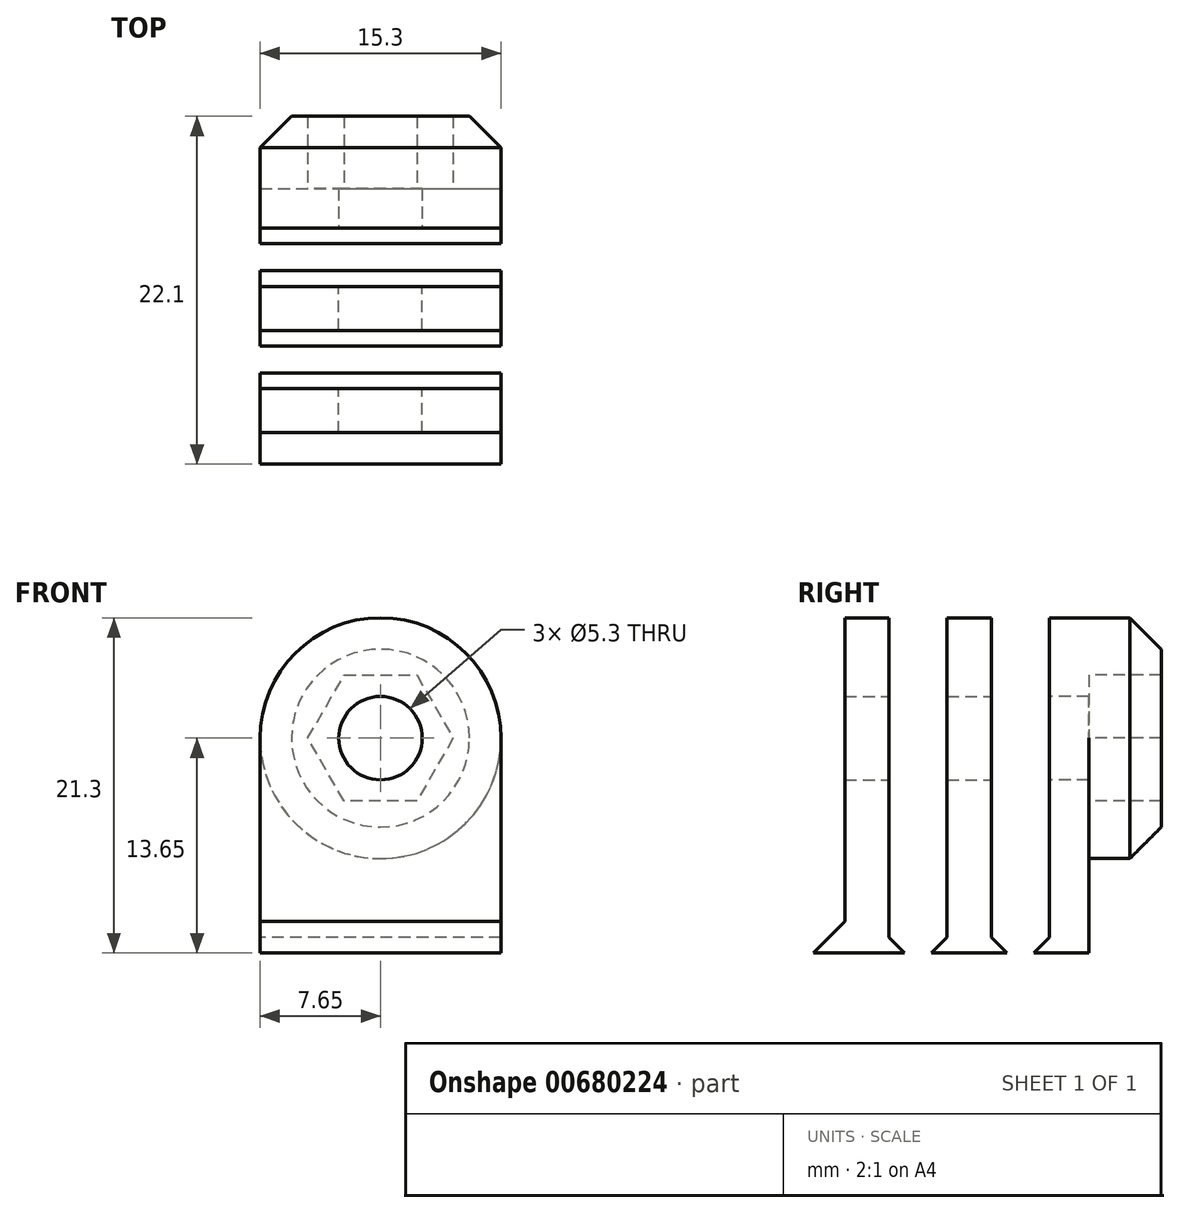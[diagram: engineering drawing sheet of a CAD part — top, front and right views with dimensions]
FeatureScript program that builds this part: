
annotation { "Feature Type Name" : "Feature", "Feature Type Description" : "" }
export const myFeature = defineFeature(function(context is Context, id is Id, definition is map)
    precondition{}
    {
        {
            var Q0;
            Q0=qCreatedBy(makeId("Front.planeOp"),FACE);
            var sketch = newSketch(context, id + "F0", { "sketchPlane" : qUnion([Q0])});
            skCircle(sketch, "E0", {"center": v(0, 0) * mm, "radius": 2.65 * mm});
            skCircle(sketch, "E1", {"center": v(0, 0) * mm, "radius": 7.65 * mm});
            skCircle(sketch, "E2.cCircle", {"center": v(0, 0) * mm, "radius": 4 * mm, "construction": true});
            skLineSegment(sketch, "E2.0", {"start": v(4.62, 0) * mm, "end": v(2.3, -4) * mm});
            skLineSegment(sketch, "E2.1", {"start": v(2.3, -4) * mm, "end": v(-2.3, -4) * mm});
            skLineSegment(sketch, "E2.2", {"start": v(-2.3, -4) * mm, "end": v(-4.62, 0) * mm});
            skLineSegment(sketch, "E2.3", {"start": v(-4.62, 0) * mm, "end": v(-2.3, 4) * mm});
            skLineSegment(sketch, "E2.4", {"start": v(-2.3, 4) * mm, "end": v(2.3, 4) * mm});
            skLineSegment(sketch, "E2.5", {"start": v(2.3, 4) * mm, "end": v(4.62, 0) * mm});
            skPoint(sketch, "E2.0.midPoint", {"position": v(3.46, -2) * mm});
            skLineSegment(sketch, "E3.top", {"start": v(-7.65, -13.65) * mm, "end": v(7.65, -13.65) * mm});
            skPoint(sketch, "E4.start.orphan", {"position": v(-7.65, 0) * mm});
            skPoint(sketch, "E5.start.orphan", {"position": v(7.65, 0) * mm});
            skLineSegment(sketch, "E6", {"start": v(-7.65, 0) * mm, "end": v(-7.65, -13.65) * mm});
            skLineSegment(sketch, "E7", {"start": v(7.65, -13.65) * mm, "end": v(7.65, 0) * mm});
            skSolve(sketch);
        }
        {
            var Q0;
            {var subQ0=sQuery(id+"F0.wireOp",EDGE,"E4");Q0=makeQuery(id+"F0.imprint","IMPRINT",FACE,{"disambiguationData":[TD([[makeQuery(id+"F0.imprint","IMPRINT",EDGE,{"derivedFrom":subQ0}),1.0]])]});}
            var Q1;
            Q1=makeQuery(id+"F0.imprint","IMPRINT",FACE,{"disambiguationData":[TD([[makeQuery(id+"F0.imprint","IMPRINT",EDGE,{"derivedFrom":sQuery(id+"F0.wireOp",EDGE,"E2.0")}),1.0]])]});
            var Q2;
            Q2=makeQuery(id+"F0.imprint","IMPRINT",FACE,{"disambiguationData":[TD([[makeQuery(id+"F0.imprint","IMPRINT",EDGE,{"derivedFrom":sQuery(id+"F0.wireOp",EDGE,"E0")}),-1.0]])]});
            var Q3;
            Q3=makeQuery(id+"F0.imprint","IMPRINT",FACE,{"disambiguationData":[TD([[makeQuery(id+"F0.imprint","IMPRINT",EDGE,{"derivedFrom":sQuery(id+"F0.wireOp",EDGE,"E3.top")}),1.0]])]});
            extrude(context, id + "F1", {"entities" : qUnion([Q0, Q1, Q2, Q3]), "endBound" : BoundingType.SYMMETRIC, "depth" : 2.8 * mm, "offsetDistance" : 25 * mm});
        }
        {
            var Q0;
            {var subQ0=sQuery(id+"F0.wireOp",EDGE,"E4");Q0=makeQuery(id+"F0.imprint","IMPRINT",FACE,{"disambiguationData":[TD([[makeQuery(id+"F0.imprint","IMPRINT",EDGE,{"derivedFrom":subQ0}),1.0]])]});}
            var Q1;
            Q1=makeQuery(id+"F0.imprint","IMPRINT",FACE,{"disambiguationData":[TD([[makeQuery(id+"F0.imprint","IMPRINT",EDGE,{"derivedFrom":sQuery(id+"F0.wireOp",EDGE,"E2.0")}),1.0]])]});
            var Q2;
            Q2=makeQuery(id+"F0.imprint","IMPRINT",FACE,{"disambiguationData":[TD([[makeQuery(id+"F0.imprint","IMPRINT",EDGE,{"derivedFrom":sQuery(id+"F0.wireOp",EDGE,"E0")}),-1.0]])]});
            var Q3;
            Q3=makeQuery(id+"F0.imprint","IMPRINT",FACE,{"disambiguationData":[TD([[makeQuery(id+"F0.imprint","IMPRINT",EDGE,{"derivedFrom":sQuery(id+"F0.wireOp",EDGE,"E3.top")}),1.0]])]});
            extrude(context, id + "F2", {"entities" : qUnion([Q0, Q1, Q2, Q3]), "depth" : 7.9 * mm, "hasSecondDirection" : true, "secondDirectionOppositeDirection" : false, "secondDirectionDepth" : 5.1 * mm, "offsetDistance" : 25 * mm});
        }
        {
            var Q0;
            Q0=makeQuery(id+"F0.imprint","IMPRINT",FACE,{"disambiguationData":[TD([[makeQuery(id+"F0.imprint","IMPRINT",EDGE,{"derivedFrom":sQuery(id+"F0.wireOp",EDGE,"E2.0")}),1.0]])]});
            var Q1;
            {var subQ0=sQuery(id+"F0.wireOp",EDGE,"E4");Q1=makeQuery(id+"F0.imprint","IMPRINT",FACE,{"disambiguationData":[TD([[makeQuery(id+"F0.imprint","IMPRINT",EDGE,{"derivedFrom":subQ0}),1.0]])]});}
            var Q2;
            Q2=makeQuery(id+"F0.imprint","IMPRINT",FACE,{"disambiguationData":[TD([[makeQuery(id+"F0.imprint","IMPRINT",EDGE,{"derivedFrom":sQuery(id+"F0.wireOp",EDGE,"E0")}),-1.0]])]});
            var Q3;
            Q3=makeQuery(id+"F0.imprint","IMPRINT",FACE,{"disambiguationData":[TD([[makeQuery(id+"F0.imprint","IMPRINT",EDGE,{"derivedFrom":sQuery(id+"F0.wireOp",EDGE,"E3.top")}),1.0]])]});
            extrude(context, id + "F3", {"entities" : qUnion([Q0, Q1, Q2, Q3]), "oppositeDirection" : true, "depth" : 7.6 * mm, "hasSecondDirection" : true, "secondDirectionOppositeDirection" : true, "secondDirectionDepth" : 5.1 * mm, "offsetDistance" : 25 * mm});
        }
        {
            var Q0;
            Q0=makeQuery(id+"F0.imprint","IMPRINT",FACE,{"disambiguationData":[TD([[makeQuery(id+"F0.imprint","IMPRINT",EDGE,{"derivedFrom":sQuery(id+"F0.wireOp",EDGE,"E2.0")}),1.0]])]});
            extrude(context, id + "F4", {"entities" : qUnion([Q0]), "operationType" : NewBodyOperationType.ADD, "oppositeDirection" : true, "depth" : 12.2 * mm, "hasSecondDirection" : true, "secondDirectionOppositeDirection" : true, "secondDirectionDepth" : 7.5 * mm});
        }
        {
            var Q0;
            Q0=makeQuery(id+"F4.opExtrude","CAP_EDGE",EDGE,{"disambiguationData":[OSD([sQuery(id+"F0.wireOp",EDGE,"E1")])],"isStart":false});
            chamfer(context, id + "F5", {"entities" : qUnion([Q0]), "width" : 2 * mm, "tangentPropagation" : true});
        }
        {
            var Q0;
            Q0=makeQuery(id+"F3.opExtrude","SWEPT_FACE",FACE,{"disambiguationData":[OSD([sQuery(id+"F0.wireOp",EDGE,"E6")])]});
            var sketch = newSketch(context, id + "F6", { "sketchPlane" : qUnion([Q0])});
            skLineSegment(sketch, "E8", {"start": v(-7.6, -13.65) * mm, "end": v(-9.6, -13.65) * mm});
            skLineSegment(sketch, "E9", {"start": v(-9.6, -13.65) * mm, "end": v(-7.6, -13.65) * mm});
            skLineSegment(sketch, "E10", {"start": v(-9.6, -13.65) * mm, "end": v(-7.6, -11.65) * mm});
            skLineSegment(sketch, "E11", {"start": v(-7.6, -11.65) * mm, "end": v(-7.6, -13.65) * mm});
            skSolve(sketch);
        }
        {
            var Q0;
            Q0=makeQuery(id+"F2.opExtrude","SWEPT_FACE",FACE,{"disambiguationData":[OSD([sQuery(id+"F0.wireOp",EDGE,"E6")])]});
            var sketch = newSketch(context, id + "F7", { "sketchPlane" : qUnion([Q0])});
            skLineSegment(sketch, "E12", {"start": v(7.9, -13.65) * mm, "end": v(9.9, -13.65) * mm});
            skLineSegment(sketch, "E13", {"start": v(9.9, -13.65) * mm, "end": v(7.9, -11.65) * mm});
            skLineSegment(sketch, "E14", {"start": v(7.9, -11.65) * mm, "end": v(7.9, -13.65) * mm});
            skSolve(sketch);
        }
        {
            var Q0;
            Q0=makeQuery(id+"F10.boolean.opBoolean","MERGE",FACE,{"derivedFrom":[makeQuery(id+"F3.opExtrude","SWEPT_FACE",FACE,{"disambiguationData":[OSD([sQuery(id+"F0.wireOp",EDGE,"E6")])]}),makeQuery(id+"F10.opExtrude","CAP_FACE",FACE,{"disambiguationData":[OSD([sQuery(id+"F6.wireOp",EDGE,"E9"),sQuery(id+"F6.wireOp",EDGE,"E10"),sQuery(id+"F6.wireOp",EDGE,"E11")])],"isStart":true})]});
            var sketch = newSketch(context, id + "F8", { "sketchPlane" : qUnion([Q0])});
            skLineSegment(sketch, "E15", {"start": v(-5.1, -13.65) * mm, "end": v(-4.1, -13.65) * mm});
            skLineSegment(sketch, "E16", {"start": v(-4.1, -13.65) * mm, "end": v(-5.1, -12.65) * mm});
            skLineSegment(sketch, "E17", {"start": v(-5.1, -12.65) * mm, "end": v(-5.1, -13.65) * mm});
            skSolve(sketch);
        }
        {
            var Q0;
            Q0=makeQuery(id+"F1.opExtrude","SWEPT_FACE",FACE,{"disambiguationData":[OSD([sQuery(id+"F0.wireOp",EDGE,"E6")])]});
            var sketch = newSketch(context, id + "F9", { "sketchPlane" : qUnion([Q0])});
            skLineSegment(sketch, "E18", {"start": v(-1.4, -13.65) * mm, "end": v(-2.4, -13.65) * mm});
            skLineSegment(sketch, "E19", {"start": v(-2.4, -13.65) * mm, "end": v(-1.4, -12.65) * mm});
            skLineSegment(sketch, "E20", {"start": v(-1.4, -12.65) * mm, "end": v(-1.4, -13.65) * mm});
            skLineSegment(sketch, "E21", {"start": v(1.4, -13.65) * mm, "end": v(2.4, -13.65) * mm});
            skLineSegment(sketch, "E22", {"start": v(2.4, -13.65) * mm, "end": v(1.4, -12.65) * mm});
            skLineSegment(sketch, "E23", {"start": v(1.4, -12.65) * mm, "end": v(1.4, -13.65) * mm});
            skLineSegment(sketch, "E24", {"start": v(5.1, -13.65) * mm, "end": v(4.1, -13.65) * mm});
            skLineSegment(sketch, "E25", {"start": v(5.1, -13.65) * mm, "end": v(5.1, -12.65) * mm});
            skLineSegment(sketch, "E26", {"start": v(5.1, -12.65) * mm, "end": v(4.1, -13.65) * mm});
            skSolve(sketch);
        }
        {
            var Q0;
            Q0=makeQuery(id+"F6.imprint","IMPRINT",FACE,{"disambiguationData":[TD([[makeQuery(id+"F6.imprint","IMPRINT",EDGE,{"derivedFrom":sQuery(id+"F6.wireOp",EDGE,"E9")}),1.0]])]});
            var Q1;
            Q1=makeQuery(id+"F7.imprint","IMPRINT",FACE,{"disambiguationData":[TD([[makeQuery(id+"F7.imprint","IMPRINT",EDGE,{"derivedFrom":sQuery(id+"F7.wireOp",EDGE,"E12")}),1.0]])]});
            var Q2;
            Q2=makeQuery(id+"F8.imprint","IMPRINT",FACE,{"disambiguationData":[TD([[makeQuery(id+"F8.imprint","IMPRINT",EDGE,{"derivedFrom":sQuery(id+"F8.wireOp",EDGE,"E15")}),1.0]])]});
            var Q3;
            Q3=makeQuery(id+"F9.imprint","IMPRINT",FACE,{"disambiguationData":[TD([[makeQuery(id+"F9.imprint","IMPRINT",EDGE,{"derivedFrom":sQuery(id+"F9.wireOp",EDGE,"E18")}),-1.0]])]});
            var Q4;
            Q4=makeQuery(id+"F9.imprint","IMPRINT",FACE,{"disambiguationData":[TD([[makeQuery(id+"F9.imprint","IMPRINT",EDGE,{"derivedFrom":sQuery(id+"F9.wireOp",EDGE,"E21")}),1.0]])]});
            var Q5;
            Q5=makeQuery(id+"F9.imprint","IMPRINT",FACE,{"disambiguationData":[TD([[makeQuery(id+"F9.imprint","IMPRINT",EDGE,{"derivedFrom":sQuery(id+"F9.wireOp",EDGE,"E24")}),-1.0]])]});
            var Q6;
            Q6=makeQuery(id+"F3.opExtrude","SWEPT_FACE",FACE,{"disambiguationData":[OSD([sQuery(id+"F0.wireOp",EDGE,"E7")])]});
            extrude(context, id + "F10", {"entities" : qUnion([Q0, Q1, Q2, Q3, Q4, Q5]), "operationType" : NewBodyOperationType.ADD, "endBound" : BoundingType.UP_TO_SURFACE, "oppositeDirection" : true, "depth" : 15.25 * mm, "endBoundEntityFace" : qUnion([Q6]), "offsetDistance" : 25 * mm});
        }
    });
